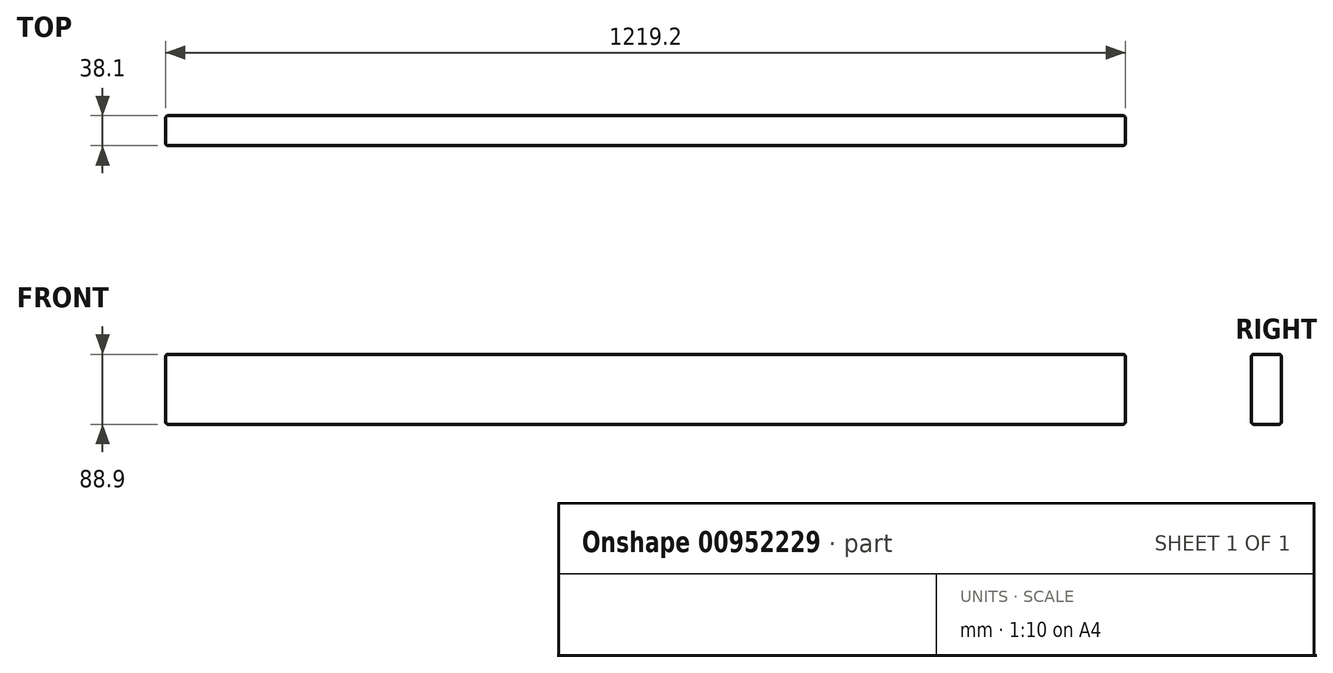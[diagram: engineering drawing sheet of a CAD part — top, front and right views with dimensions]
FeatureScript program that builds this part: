
annotation { "Feature Type Name" : "Feature", "Feature Type Description" : "" }
export const myFeature = defineFeature(function(context is Context, id is Id, definition is map)
    precondition{}
    {
        {
            var Q0;
            Q0=qCreatedBy(makeId("Front.planeOp"),FACE);
            var sketch = newSketch(context, id + "F0", { "sketchPlane" : qUnion([Q0])});
            skLineSegment(sketch, "E0.bottom", {"start": v(1219.2, 0) * mm, "end": v(0, 0) * mm});
            skLineSegment(sketch, "E0.top", {"start": v(1219.2, -88.9) * mm, "end": v(0, -88.9) * mm});
            skLineSegment(sketch, "E0.left", {"start": v(1219.2, 0) * mm, "end": v(1219.2, -88.9) * mm});
            skLineSegment(sketch, "E0.right", {"start": v(0, 0) * mm, "end": v(0, -88.9) * mm});
            skSolve(sketch);
        }
        {
            var Q0;
            Q0 = qSketchRegion(id + "F0", true);
            extrude(context, id + "F1", {"entities" : qUnion([Q0]), "depth" : 38.1 * mm, "offsetDistance" : 25.4 * mm});
        }
        {
            var Q0;
            Q0=makeQuery(id+"F1.opExtrude","CAP_EDGE",EDGE,{"disambiguationData":[OSD([sQuery(id+"F0.wireOp",EDGE,"E0.bottom")])],"isStart":false});
            var Q1;
            Q1=makeQuery(id+"F1.opExtrude","CAP_EDGE",EDGE,{"disambiguationData":[OSD([sQuery(id+"F0.wireOp",EDGE,"E0.bottom")])],"isStart":true});
            var Q2;
            Q2=makeQuery(id+"F1.opExtrude","CAP_EDGE",EDGE,{"disambiguationData":[OSD([sQuery(id+"F0.wireOp",EDGE,"E0.top")])],"isStart":false});
            var Q3;
            Q3=makeQuery(id+"F1.opExtrude","CAP_EDGE",EDGE,{"disambiguationData":[OSD([sQuery(id+"F0.wireOp",EDGE,"E0.right")])],"isStart":false});
            var Q4;
            Q4=makeQuery(id+"F1.opExtrude","CAP_EDGE",EDGE,{"disambiguationData":[OSD([sQuery(id+"F0.wireOp",EDGE,"E0.right")])],"isStart":true});
            var Q5;
            Q5=makeQuery(id+"F1.opExtrude","SWEPT_EDGE",EDGE,{"disambiguationData":[OSD([sQuery(id+"F0.wireOp",EDGE,"E0.top"),sQuery(id+"F0.wireOp",EDGE,"E0.right")])]});
            var Q6;
            Q6=makeQuery(id+"F1.opExtrude","SWEPT_EDGE",EDGE,{"disambiguationData":[OSD([sQuery(id+"F0.wireOp",EDGE,"E0.bottom"),sQuery(id+"F0.wireOp",EDGE,"E0.right")])]});
            var Q7;
            Q7=makeQuery(id+"F1.opExtrude","CAP_EDGE",EDGE,{"disambiguationData":[OSD([sQuery(id+"F0.wireOp",EDGE,"E0.top")])],"isStart":true});
            var Q8;
            Q8=makeQuery(id+"F1.opExtrude","CAP_EDGE",EDGE,{"disambiguationData":[OSD([sQuery(id+"F0.wireOp",EDGE,"E0.left")])],"isStart":true});
            var Q9;
            Q9=makeQuery(id+"F1.opExtrude","SWEPT_EDGE",EDGE,{"disambiguationData":[OSD([sQuery(id+"F0.wireOp",EDGE,"E0.bottom"),sQuery(id+"F0.wireOp",EDGE,"E0.left")])]});
            var Q10;
            Q10=makeQuery(id+"F1.opExtrude","CAP_EDGE",EDGE,{"disambiguationData":[OSD([sQuery(id+"F0.wireOp",EDGE,"E0.left")])],"isStart":false});
            var Q11;
            Q11=makeQuery(id+"F1.opExtrude","SWEPT_EDGE",EDGE,{"disambiguationData":[OSD([sQuery(id+"F0.wireOp",EDGE,"E0.top"),sQuery(id+"F0.wireOp",EDGE,"E0.left")])]});
            fillet(context, id + "F2", {"entities" : qUnion([Q0, Q1, Q2, Q3, Q4, Q5, Q6, Q7, Q8, Q9, Q10, Q11]), "radius" : 3.17 * mm, "tangentPropagation" : true, "allowEdgeOverflow" : false});
        }
    });
